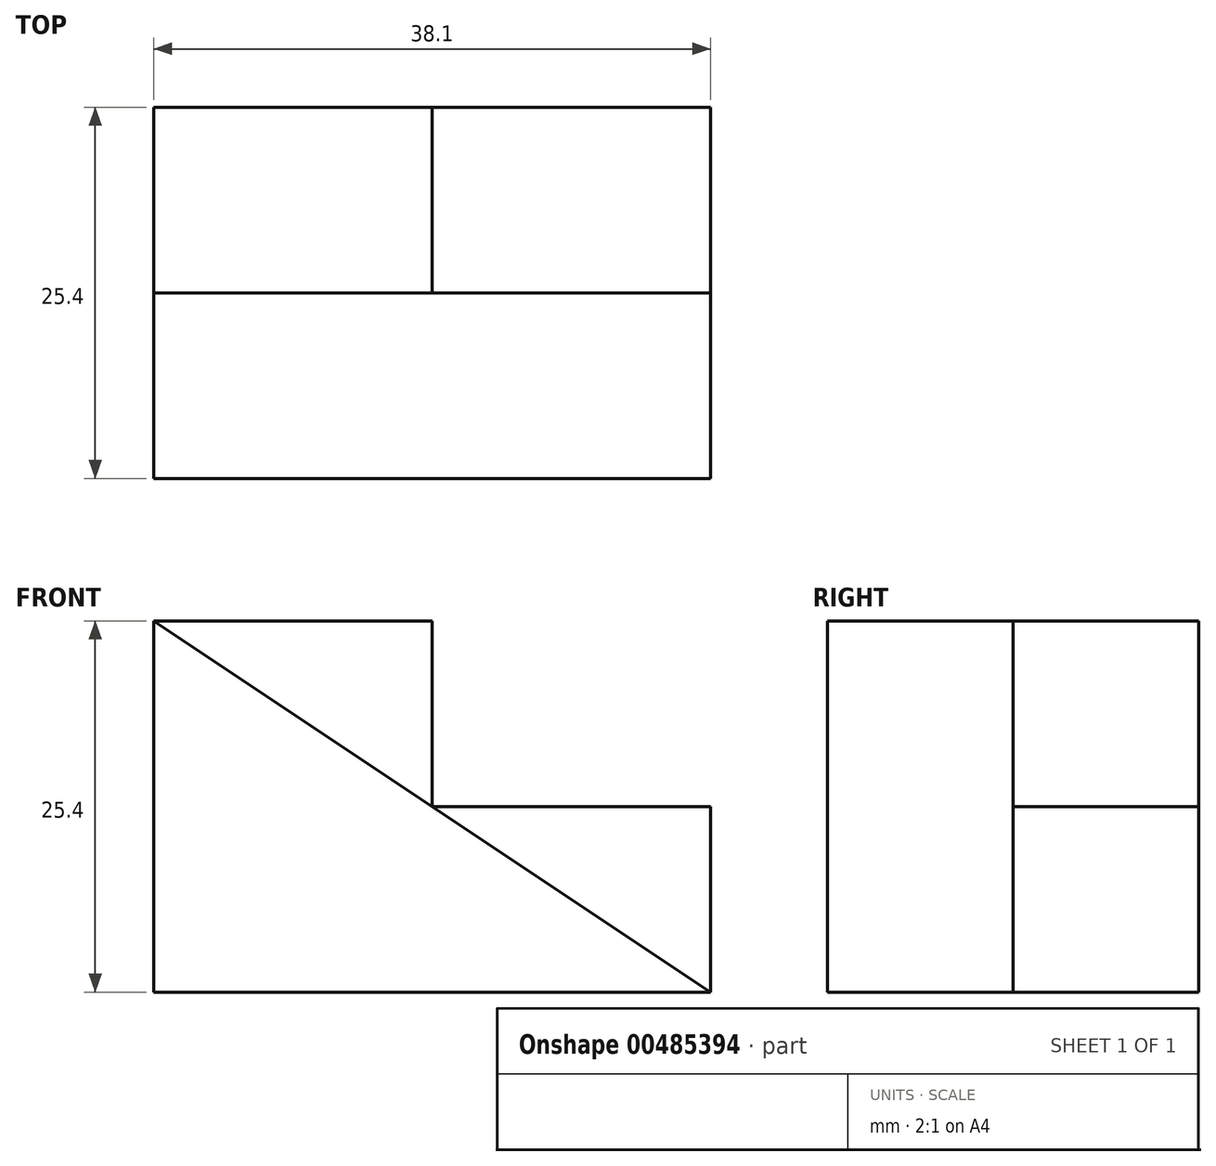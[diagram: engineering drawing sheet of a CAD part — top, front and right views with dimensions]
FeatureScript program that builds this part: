
annotation { "Feature Type Name" : "Feature", "Feature Type Description" : "" }
export const myFeature = defineFeature(function(context is Context, id is Id, definition is map)
    precondition{}
    {
        {
            var Q0;
            Q0=qCreatedBy(makeId("Front.planeOp"),FACE);
            var sketch = newSketch(context, id + "F0", { "sketchPlane" : qUnion([Q0])});
            skLineSegment(sketch, "E0.bottom", {"start": v(0, 0) * mm, "end": v(0, 0) * mm});
            skLineSegment(sketch, "E0.top", {"start": v(0, 25.4) * mm, "end": v(0, 25.4) * mm});
            skLineSegment(sketch, "E0.left", {"start": v(0, 0) * mm, "end": v(0, 25.4) * mm});
            skLineSegment(sketch, "E0.right", {"start": v(0, 0) * mm, "end": v(0, 25.4) * mm});
            skLineSegment(sketch, "E1", {"start": v(0, 0) * mm, "end": v(38.1, 0) * mm});
            skLineSegment(sketch, "E2", {"start": v(38.1, 0) * mm, "end": v(0, 25.4) * mm});
            skSolve(sketch);
        }
        {
            var Q0;
            Q0 = qSketchRegion(id + "F0", true);
            var Q1;
            Q1=makeQuery(id+"F0.imprint","IMPRINT",FACE,{"disambiguationData":[TD([[makeQuery(id+"F0.imprint","IMPRINT",EDGE,{"derivedFrom":sQuery(id+"F0.wireOp",EDGE,"E0.right")}),-1.0]])]});
            extrude(context, id + "F1", {"entities" : qUnion([Q0, Q1]), "depth" : 12.7 * mm});
        }
        {
            var Q0;
            Q0=qCreatedBy(makeId("Front.planeOp"),FACE);
            var sketch = newSketch(context, id + "F2", { "sketchPlane" : qUnion([Q0])});
            skLineSegment(sketch, "E3", {"start": v(0, 25.4) * mm, "end": v(19.05, 25.4) * mm});
            skLineSegment(sketch, "E4", {"start": v(19.05, 25.4) * mm, "end": v(19.05, 12.7) * mm});
            skLineSegment(sketch, "E5", {"start": v(19.05, 12.7) * mm, "end": v(38.1, 12.7) * mm});
            skLineSegment(sketch, "E6", {"start": v(38.1, 12.7) * mm, "end": v(38.1, 0) * mm});
            skLineSegment(sketch, "E7", {"start": v(0, 25.4) * mm, "end": v(0, 0) * mm});
            skLineSegment(sketch, "E8", {"start": v(0, 0) * mm, "end": v(38.1, 0) * mm});
            skSolve(sketch);
        }
        {
            var Q0;
            Q0 = qSketchRegion(id + "F2", true);
            extrude(context, id + "F3", {"entities" : qUnion([Q0]), "operationType" : NewBodyOperationType.ADD, "oppositeDirection" : true, "depth" : 12.7 * mm});
        }
    });
